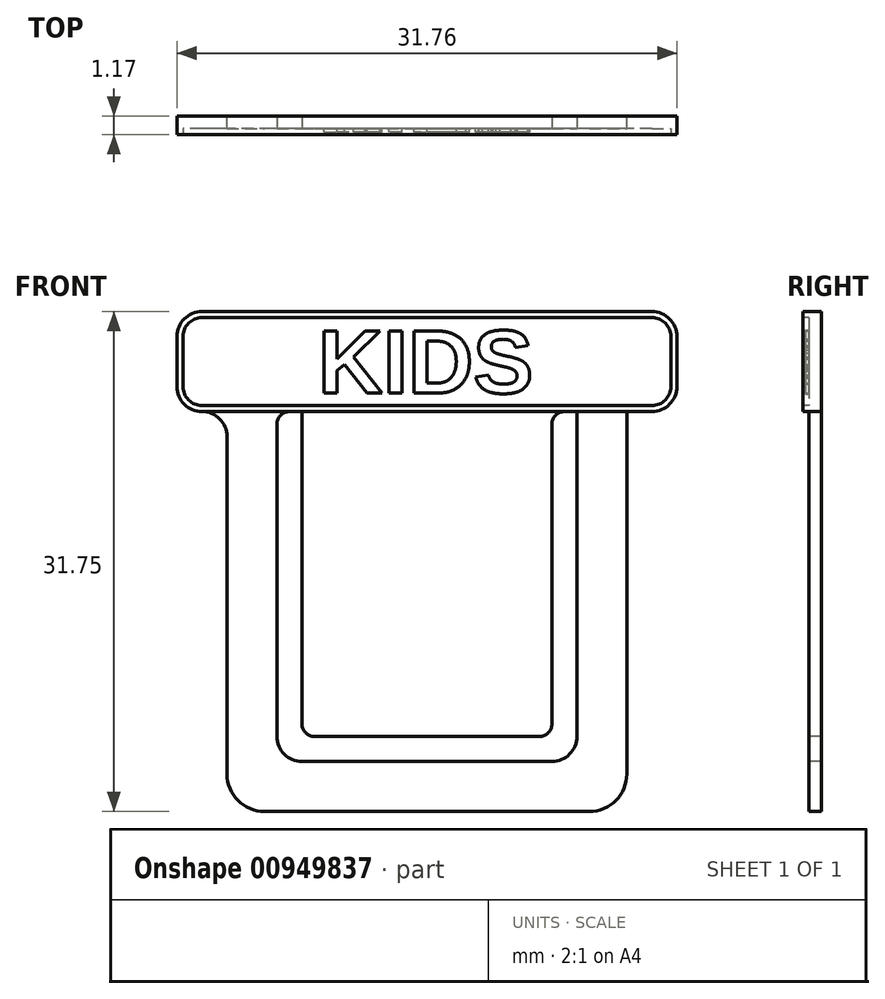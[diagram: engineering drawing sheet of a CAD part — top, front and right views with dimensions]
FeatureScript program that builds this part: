
annotation { "Feature Type Name" : "Feature", "Feature Type Description" : "" }
export const myFeature = defineFeature(function(context is Context, id is Id, definition is map)
    precondition{}
    {
        {
            var Q0;
            Q0=qCreatedBy(makeId("Front.planeOp"),FACE);
            var sketch = newSketch(context, id + "F0", { "sketchPlane" : qUnion([Q0])});
            skLineSegment(sketch, "E0.bottom", {"start": v(12.7, 12.7) * mm, "end": v(-12.7, 12.7) * mm});
            skLineSegment(sketch, "E0.top", {"start": v(12.7, -12.7) * mm, "end": v(-12.7, -12.7) * mm});
            skLineSegment(sketch, "E0.left", {"start": v(12.7, 12.7) * mm, "end": v(12.7, -12.7) * mm});
            skLineSegment(sketch, "E0.right", {"start": v(-12.7, 12.7) * mm, "end": v(-12.7, -12.7) * mm});
            skPoint(sketch, "E0.middle", {"position": v(0, 0) * mm});
            skSolve(sketch);
        }
        {
            var Q0;
            Q0=makeQuery(id+"F0.imprint","IMPRINT",FACE,{"disambiguationData":[TD([[makeQuery(id+"F0.imprint","IMPRINT",EDGE,{"derivedFrom":sQuery(id+"F0.wireOp",EDGE,"E0.bottom")}),1.0]])]});
            extrude(context, id + "F1", {"entities" : qUnion([Q0]), "depth" : 0.8 * mm, "offsetDistance" : 25.4 * mm});
        }
        {
            var Q0;
            Q0=makeQuery(id+"F1.opExtrude","SWEPT_EDGE",EDGE,{"disambiguationData":[OSD([sQuery(id+"F0.wireOp",EDGE,"E0.top"),sQuery(id+"F0.wireOp",EDGE,"E0.left")])]});
            var Q1;
            Q1=makeQuery(id+"F1.opExtrude","SWEPT_EDGE",EDGE,{"disambiguationData":[OSD([sQuery(id+"F0.wireOp",EDGE,"E0.top"),sQuery(id+"F0.wireOp",EDGE,"E0.right")])]});
            fillet(context, id + "F2", {"entities" : qUnion([Q0, Q1]), "radius" : 2.38 * mm, "tangentPropagation" : true, "allowEdgeOverflow" : false});
        }
        {
            var Q0;
            Q0=makeQuery(id+"F1.opExtrude","CAP_FACE",FACE,{"disambiguationData":[OSD([sQuery(id+"F0.wireOp",EDGE,"E0.bottom"),sQuery(id+"F0.wireOp",EDGE,"E0.top"),sQuery(id+"F0.wireOp",EDGE,"E0.left"),sQuery(id+"F0.wireOp",EDGE,"E0.right")])],"isStart":false});
            var sketch = newSketch(context, id + "F3", { "sketchPlane" : qUnion([Q0])});
            skLineSegment(sketch, "E1.bottom", {"start": v(9.52, 12.7) * mm, "end": v(-9.53, 12.7) * mm});
            skLineSegment(sketch, "E1.top", {"start": v(9.53, -9.53) * mm, "end": v(-9.52, -9.53) * mm});
            skLineSegment(sketch, "E1.left", {"start": v(9.52, 12.7) * mm, "end": v(9.53, -9.53) * mm});
            skLineSegment(sketch, "E1.right", {"start": v(-9.53, 12.7) * mm, "end": v(-9.52, -9.53) * mm});
            skPoint(sketch, "E1.middle", {"position": v(0, 0) * mm});
            skSolve(sketch);
        }
        {
            var Q0;
            Q0=makeQuery(id+"F3.imprint","IMPRINT",FACE,{"disambiguationData":[TD([[makeQuery(id+"F3.imprint","IMPRINT",EDGE,{"derivedFrom":sQuery(id+"F3.wireOp",EDGE,"E1.bottom")}),1.0]])]});
            extrude(context, id + "F4", {"entities" : qUnion([Q0]), "operationType" : NewBodyOperationType.REMOVE, "oppositeDirection" : true, "depth" : 4.93 * mm, "offsetDistance" : 25.4 * mm});
        }
        {
            var Q0;
            Q0=makeQuery(id+"F1.opExtrude","CAP_FACE",FACE,{"disambiguationData":[OSD([sQuery(id+"F0.wireOp",EDGE,"E0.bottom"),sQuery(id+"F0.wireOp",EDGE,"E0.top"),sQuery(id+"F0.wireOp",EDGE,"E0.left"),sQuery(id+"F0.wireOp",EDGE,"E0.right")])],"isStart":false});
            var sketch = newSketch(context, id + "F5", { "sketchPlane" : qUnion([Q0])});
            skLineSegment(sketch, "E2.bottom", {"start": v(-15.88, 12.7) * mm, "end": v(15.88, 12.7) * mm});
            skLineSegment(sketch, "E2.top", {"start": v(-15.88, 19.05) * mm, "end": v(15.88, 19.05) * mm});
            skLineSegment(sketch, "E2.left", {"start": v(-15.88, 12.7) * mm, "end": v(-15.88, 19.05) * mm});
            skLineSegment(sketch, "E2.right", {"start": v(15.87, 12.7) * mm, "end": v(15.87, 19.05) * mm});
            skSolve(sketch);
        }
        {
            var Q0;
            Q0=makeQuery(id+"F5.imprint","IMPRINT",FACE,{"disambiguationData":[TD([[makeQuery(id+"F5.imprint","IMPRINT",EDGE,{"derivedFrom":sQuery(id+"F5.wireOp",EDGE,"E2.top")}),-1.0]])]});
            extrude(context, id + "F6", {"entities" : qUnion([Q0]), "operationType" : NewBodyOperationType.ADD, "oppositeDirection" : true, "depth" : 0.8 * mm, "offsetDistance" : 25.4 * mm});
        }
        {
            var Q0;
            Q0=makeQuery(id+"F6.opExtrude","SWEPT_EDGE",EDGE,{"disambiguationData":[OSD([sQuery(id+"F5.wireOp",EDGE,"E2.top"),sQuery(id+"F5.wireOp",EDGE,"E2.left")])]});
            var Q1;
            Q1=makeQuery(id+"F6.opExtrude","SWEPT_EDGE",EDGE,{"disambiguationData":[OSD([sQuery(id+"F5.wireOp",EDGE,"E2.top"),sQuery(id+"F5.wireOp",EDGE,"E2.right")])]});
            var Q2;
            Q2=makeQuery(id+"F6.opExtrude","SWEPT_EDGE",EDGE,{"disambiguationData":[OSD([sQuery(id+"F5.wireOp",EDGE,"E2.bottom"),sQuery(id+"F5.wireOp",EDGE,"E2.right")])]});
            var Q3;
            Q3=makeQuery(id+"F1.opExtrude","SWEPT_EDGE",EDGE,{"disambiguationData":[OSD([sQuery(id+"F0.wireOp",EDGE,"E0.bottom"),sQuery(id+"F0.wireOp",EDGE,"E0.left")])]});
            var Q4;
            Q4=makeQuery(id+"F6.opExtrude","SWEPT_EDGE",EDGE,{"disambiguationData":[OSD([sQuery(id+"F5.wireOp",EDGE,"E2.bottom"),sQuery(id+"F5.wireOp",EDGE,"E2.left")])]});
            var Q5;
            Q5=makeQuery(id+"F1.opExtrude","SWEPT_EDGE",EDGE,{"disambiguationData":[OSD([sQuery(id+"F0.wireOp",EDGE,"E0.bottom"),sQuery(id+"F0.wireOp",EDGE,"E0.right")])]});
            fillet(context, id + "F7", {"entities" : qUnion([Q0, Q1, Q2, Q3, Q4, Q5]), "radius" : 1.59 * mm, "tangentPropagation" : true, "allowEdgeOverflow" : false});
        }
        {
            var Q0;
            Q0=makeQuery(id+"F4.boolean.opBoolean","COPY",EDGE,{"derivedFrom":makeQuery(id+"F4.opExtrude","SWEPT_EDGE",EDGE,{"disambiguationData":[OSD([sQuery(id+"F3.wireOp",EDGE,"E1.top"),sQuery(id+"F3.wireOp",EDGE,"E1.right")])]})});
            var Q1;
            Q1=makeQuery(id+"F4.boolean.opBoolean","COPY",EDGE,{"derivedFrom":makeQuery(id+"F4.opExtrude","SWEPT_EDGE",EDGE,{"disambiguationData":[OSD([sQuery(id+"F3.wireOp",EDGE,"E1.top"),sQuery(id+"F3.wireOp",EDGE,"E1.left")])]})});
            fillet(context, id + "F8", {"entities" : qUnion([Q0, Q1]), "radius" : 1.59 * mm, "tangentPropagation" : true, "allowEdgeOverflow" : false});
        }
        {
            var Q0;
            Q0=makeQuery(id+"F6.boolean.opBoolean","MERGE",FACE,{"derivedFrom":[makeQuery(id+"F1.opExtrude","CAP_FACE",FACE,{"disambiguationData":[OSD([sQuery(id+"F0.wireOp",EDGE,"E0.bottom"),sQuery(id+"F0.wireOp",EDGE,"E0.top"),sQuery(id+"F0.wireOp",EDGE,"E0.left"),sQuery(id+"F0.wireOp",EDGE,"E0.right")])],"isStart":false}),makeQuery(id+"F6.opExtrude","CAP_FACE",FACE,{"disambiguationData":[OSD([sQuery(id+"F5.wireOp",EDGE,"E2.bottom"),sQuery(id+"F5.wireOp",EDGE,"E2.top"),sQuery(id+"F5.wireOp",EDGE,"E2.left"),sQuery(id+"F5.wireOp",EDGE,"E2.right")])],"isStart":true})]});
            var sketch = newSketch(context, id + "F9", { "sketchPlane" : qUnion([Q0])});
            skLineSegment(sketch, "E3.bottom", {"start": v(-7.94, 12.7) * mm, "end": v(7.94, 12.7) * mm});
            skLineSegment(sketch, "E3.top", {"start": v(-7.94, -7.94) * mm, "end": v(7.94, -7.94) * mm});
            skLineSegment(sketch, "E3.left", {"start": v(-7.94, 12.7) * mm, "end": v(-7.94, -7.94) * mm});
            skLineSegment(sketch, "E3.right", {"start": v(7.94, 12.7) * mm, "end": v(7.94, -7.94) * mm});
            skSolve(sketch);
        }
        {
            var Q0;
            Q0=makeQuery(id+"F9.imprint","IMPRINT",FACE,{"disambiguationData":[TD([[makeQuery(id+"F9.imprint","IMPRINT",EDGE,{"derivedFrom":sQuery(id+"F9.wireOp",EDGE,"E3.bottom")}),1.0]])]});
            extrude(context, id + "F10", {"entities" : qUnion([Q0]), "operationType" : NewBodyOperationType.ADD, "oppositeDirection" : true, "depth" : 0.8 * mm, "offsetDistance" : 25.4 * mm});
        }
        {
            var Q0;
            Q0=makeQuery(id+"F10.opExtrude","SWEPT_EDGE",EDGE,{"disambiguationData":[OSD([sQuery(id+"F5.wireOp",EDGE,"E2.bottom"),sQuery(id+"F9.wireOp",EDGE,"E3.bottom"),sQuery(id+"F9.wireOp",EDGE,"E3.left")])]});
            var Q1;
            Q1=makeQuery(id+"F4.boolean.opBoolean","COPY",EDGE,{"derivedFrom":makeQuery(id+"F4.opExtrude","SWEPT_EDGE",EDGE,{"disambiguationData":[OSD([sQuery(id+"F0.wireOp",EDGE,"E0.bottom"),sQuery(id+"F3.wireOp",EDGE,"E1.bottom"),sQuery(id+"F3.wireOp",EDGE,"E1.right")])]})});
            var Q2;
            Q2=makeQuery(id+"F10.opExtrude","SWEPT_EDGE",EDGE,{"disambiguationData":[OSD([sQuery(id+"F5.wireOp",EDGE,"E2.bottom"),sQuery(id+"F9.wireOp",EDGE,"E3.bottom"),sQuery(id+"F9.wireOp",EDGE,"E3.right")])]});
            var Q3;
            Q3=makeQuery(id+"F4.boolean.opBoolean","COPY",EDGE,{"derivedFrom":makeQuery(id+"F4.opExtrude","SWEPT_EDGE",EDGE,{"disambiguationData":[OSD([sQuery(id+"F0.wireOp",EDGE,"E0.bottom"),sQuery(id+"F3.wireOp",EDGE,"E1.bottom"),sQuery(id+"F3.wireOp",EDGE,"E1.left")])]})});
            fillet(context, id + "F11", {"entities" : qUnion([Q0, Q1, Q2, Q3]), "radius" : 0.8 * mm, "tangentPropagation" : true, "allowEdgeOverflow" : false});
        }
        {
            var Q0;
            Q0=makeQuery(id+"F10.opExtrude","SWEPT_EDGE",EDGE,{"disambiguationData":[OSD([sQuery(id+"F9.wireOp",EDGE,"E3.top"),sQuery(id+"F9.wireOp",EDGE,"E3.left")])]});
            var Q1;
            Q1=makeQuery(id+"F10.opExtrude","SWEPT_EDGE",EDGE,{"disambiguationData":[OSD([sQuery(id+"F9.wireOp",EDGE,"E3.top"),sQuery(id+"F9.wireOp",EDGE,"E3.right")])]});
            fillet(context, id + "F12", {"entities" : qUnion([Q0, Q1]), "radius" : 0.8 * mm, "tangentPropagation" : true, "allowEdgeOverflow" : false});
        }
        {
            var Q0;
            Q0=makeQuery(id+"F10.boolean.opBoolean","MERGE",FACE,{"derivedFrom":[makeQuery(id+"F6.boolean.opBoolean","MERGE",FACE,{"derivedFrom":[makeQuery(id+"F1.opExtrude","CAP_FACE",FACE,{"disambiguationData":[OSD([sQuery(id+"F0.wireOp",EDGE,"E0.bottom"),sQuery(id+"F0.wireOp",EDGE,"E0.top"),sQuery(id+"F0.wireOp",EDGE,"E0.left"),sQuery(id+"F0.wireOp",EDGE,"E0.right")])],"isStart":false}),makeQuery(id+"F6.opExtrude","CAP_FACE",FACE,{"disambiguationData":[OSD([sQuery(id+"F5.wireOp",EDGE,"E2.bottom"),sQuery(id+"F5.wireOp",EDGE,"E2.top"),sQuery(id+"F5.wireOp",EDGE,"E2.left"),sQuery(id+"F5.wireOp",EDGE,"E2.right")])],"isStart":true})]}),makeQuery(id+"F10.opExtrude","CAP_FACE",FACE,{"disambiguationData":[OSD([sQuery(id+"F9.wireOp",EDGE,"E3.bottom"),sQuery(id+"F9.wireOp",EDGE,"E3.top"),sQuery(id+"F9.wireOp",EDGE,"E3.left"),sQuery(id+"F9.wireOp",EDGE,"E3.right")])],"isStart":true})]});
            var sketch = newSketch(context, id + "F13", { "sketchPlane" : qUnion([Q0])});
            skArc(sketch, "E4.0", {"start": v(-14.29, 19.05) * mm, "mid": v(-15.41, 18.59) * mm, "end": v(-15.88, 17.46) * mm});
            skLineSegment(sketch, "E5.0", {"start": v(-15.88, 14.29) * mm, "end": v(-15.88, 17.46) * mm});
            skArc(sketch, "E6.0", {"start": v(-15.88, 14.29) * mm, "mid": v(-15.41, 13.16) * mm, "end": v(-14.29, 12.7) * mm});
            skLineSegment(sketch, "E7.0", {"start": v(-14.29, 19.05) * mm, "end": v(14.29, 19.05) * mm});
            skArc(sketch, "E8.0", {"start": v(15.87, 17.46) * mm, "mid": v(15.41, 18.59) * mm, "end": v(14.29, 19.05) * mm});
            skLineSegment(sketch, "E9.0", {"start": v(15.87, 14.29) * mm, "end": v(15.87, 17.46) * mm});
            skArc(sketch, "E10.0", {"start": v(14.29, 12.7) * mm, "mid": v(15.41, 13.16) * mm, "end": v(15.87, 14.29) * mm});
            skLineSegment(sketch, "E11", {"start": v(-14.29, 12.7) * mm, "end": v(14.29, 12.7) * mm});
            skSolve(sketch);
        }
        {
            var Q0;
            Q0=makeQuery(id+"F13.imprint","IMPRINT",FACE,{"disambiguationData":[TD([[makeQuery(id+"F13.imprint","IMPRINT",EDGE,{"derivedFrom":sQuery(id+"F13.wireOp",EDGE,"E4.0")}),1.0]])]});
            extrude(context, id + "F14", {"entities" : qUnion([Q0]), "operationType" : NewBodyOperationType.ADD, "depth" : 0.38 * mm, "offsetDistance" : 25.4 * mm});
        }
        {
            var Q0;
            Q0=makeQuery(id+"F14.opExtrude","CAP_FACE",FACE,{"disambiguationData":[OSD([sQuery(id+"F13.wireOp",EDGE,"E4.0"),sQuery(id+"F13.wireOp",EDGE,"E5.0"),sQuery(id+"F13.wireOp",EDGE,"E6.0"),sQuery(id+"F13.wireOp",EDGE,"E7.0"),sQuery(id+"F13.wireOp",EDGE,"E8.0"),sQuery(id+"F13.wireOp",EDGE,"E9.0"),sQuery(id+"F13.wireOp",EDGE,"E10.0"),sQuery(id+"F13.wireOp",EDGE,"E11")])],"isStart":false});
            var sketch = newSketch(context, id + "F15", { "sketchPlane" : qUnion([Q0])});
            skArc(sketch, "E12.0", {"start": v(-14.29, 19.05) * mm, "mid": v(-15.41, 18.59) * mm, "end": v(-15.88, 17.46) * mm});
            skLineSegment(sketch, "E13.0", {"start": v(-14.29, 19.05) * mm, "end": v(14.29, 19.05) * mm});
            skLineSegment(sketch, "E14.0", {"start": v(-15.88, 14.29) * mm, "end": v(-15.88, 17.46) * mm});
            skArc(sketch, "E15.0", {"start": v(-15.88, 14.29) * mm, "mid": v(-15.41, 13.16) * mm, "end": v(-14.29, 12.7) * mm});
            skLineSegment(sketch, "E16.0", {"start": v(-14.29, 12.7) * mm, "end": v(14.29, 12.7) * mm});
            skArc(sketch, "E17.0", {"start": v(14.29, 12.7) * mm, "mid": v(15.41, 13.16) * mm, "end": v(15.87, 14.29) * mm});
            skArc(sketch, "E18.0", {"start": v(15.87, 17.46) * mm, "mid": v(15.41, 18.59) * mm, "end": v(14.29, 19.05) * mm});
            skArc(sketch, "E19", {"start": v(-14.29, 18.67) * mm, "mid": v(-15.14, 18.32) * mm, "end": v(-15.5, 17.46) * mm});
            skArc(sketch, "E20", {"start": v(-15.5, 14.29) * mm, "mid": v(-15.14, 13.43) * mm, "end": v(-14.29, 13.08) * mm});
            skArc(sketch, "E21", {"start": v(15.5, 17.46) * mm, "mid": v(15.14, 18.32) * mm, "end": v(14.29, 18.67) * mm});
            skArc(sketch, "E22", {"start": v(14.29, 13.08) * mm, "mid": v(15.14, 13.43) * mm, "end": v(15.5, 14.29) * mm});
            skLineSegment(sketch, "E23", {"start": v(-14.29, 19.05) * mm, "end": v(-14.29, 12.7) * mm, "construction": true});
            skLineSegment(sketch, "E24", {"start": v(-15.88, 17.46) * mm, "end": v(15.87, 17.46) * mm, "construction": true});
            skLineSegment(sketch, "E25", {"start": v(14.29, 19.05) * mm, "end": v(14.29, 12.7) * mm, "construction": true});
            skLineSegment(sketch, "E26", {"start": v(15.87, 14.29) * mm, "end": v(-15.88, 14.29) * mm, "construction": true});
            skLineSegment(sketch, "E27", {"start": v(14.29, 18.67) * mm, "end": v(-14.29, 18.67) * mm});
            skLineSegment(sketch, "E28", {"start": v(-15.5, 17.46) * mm, "end": v(-15.5, 14.29) * mm});
            skLineSegment(sketch, "E29", {"start": v(-14.29, 13.08) * mm, "end": v(14.29, 13.08) * mm});
            skLineSegment(sketch, "E30", {"start": v(15.5, 17.46) * mm, "end": v(15.5, 14.29) * mm});
            skSolve(sketch);
        }
        {
            var Q0;
            Q0=makeQuery(id+"F15.imprint","IMPRINT",FACE,{"disambiguationData":[TD([[makeQuery(id+"F15.imprint","IMPRINT",EDGE,{"derivedFrom":sQuery(id+"F15.wireOp",EDGE,"E19")}),1.0]])]});
            var Q1;
            {var subQ0=sQuery(id+"F9.wireOp",EDGE,"E3.right");var subQ1=sQuery(id+"F9.wireOp",EDGE,"E3.top");var subQ3=sQuery(id+"F0.wireOp",EDGE,"E0.bottom");var subQ4=sQuery(id+"F9.wireOp",EDGE,"E3.left");var subQ5=makeQuery(id+"F6.opExtrude","CAP_FACE",FACE,{"disambiguationData":[OSD([sQuery(id+"F5.wireOp",EDGE,"E2.bottom"),sQuery(id+"F5.wireOp",EDGE,"E2.top"),sQuery(id+"F5.wireOp",EDGE,"E2.left"),sQuery(id+"F5.wireOp",EDGE,"E2.right")])],"isStart":true});var subQ6=makeQuery(id+"F1.opExtrude","CAP_FACE",FACE,{"disambiguationData":[OSD([subQ3,sQuery(id+"F0.wireOp",EDGE,"E0.top"),sQuery(id+"F0.wireOp",EDGE,"E0.left"),sQuery(id+"F0.wireOp",EDGE,"E0.right")])],"isStart":false});var subQ7=makeQuery(id+"F10.opExtrude","CAP_FACE",FACE,{"disambiguationData":[OSD([sQuery(id+"F9.wireOp",EDGE,"E3.bottom"),subQ1,subQ4,subQ0])],"isStart":true});Q1=makeQuery(id+"F14.boolean.opBoolean","SPLIT",FACE,{"disambiguationData":[TD([makeQuery(id+"F10.opExtrude","SWEPT_FACE",FACE,{"disambiguationData":[OSD([subQ1])]})])],"derivedFrom":makeQuery(id+"F10.boolean.opBoolean","MERGE",FACE,{"derivedFrom":[makeQuery(id+"F6.boolean.opBoolean","MERGE",FACE,{"derivedFrom":[subQ6,subQ5]}),subQ7]})});}
            extrude(context, id + "F16", {"entities" : qUnion([Q0]), "operationType" : NewBodyOperationType.REMOVE, "endBound" : BoundingType.UP_TO_SURFACE, "oppositeDirection" : true, "depth" : 25.4 * mm, "endBoundEntityFace" : qUnion([Q1]), "offsetDistance" : 25.4 * mm});
        }
        {
            var Q0;
            Q0=qCreatedBy(makeId("Front.planeOp"),FACE);
            var sketch = newSketch(context, id + "F17", { "sketchPlane" : qUnion([Q0])});
            skText(sketch, "E31", { "text": "KIDS", "fontName": "Arimo-Bold.ttf"});
            const initialGuessF17  = {"E31": [-0.00692, 0.01388, 1, 0, 0.00412]};
            skSetInitialGuess(sketch, initialGuessF17);
            skSolve(sketch);
        }
        {
            var Q0;
            Q0=qSketchRegion(id+"F17",true);
            extrude(context, id + "F18", {"entities" : qUnion([Q0]), "operationType" : NewBodyOperationType.ADD, "depth" : 1.02 * mm, "offsetDistance" : 25.4 * mm});
        }
    });
